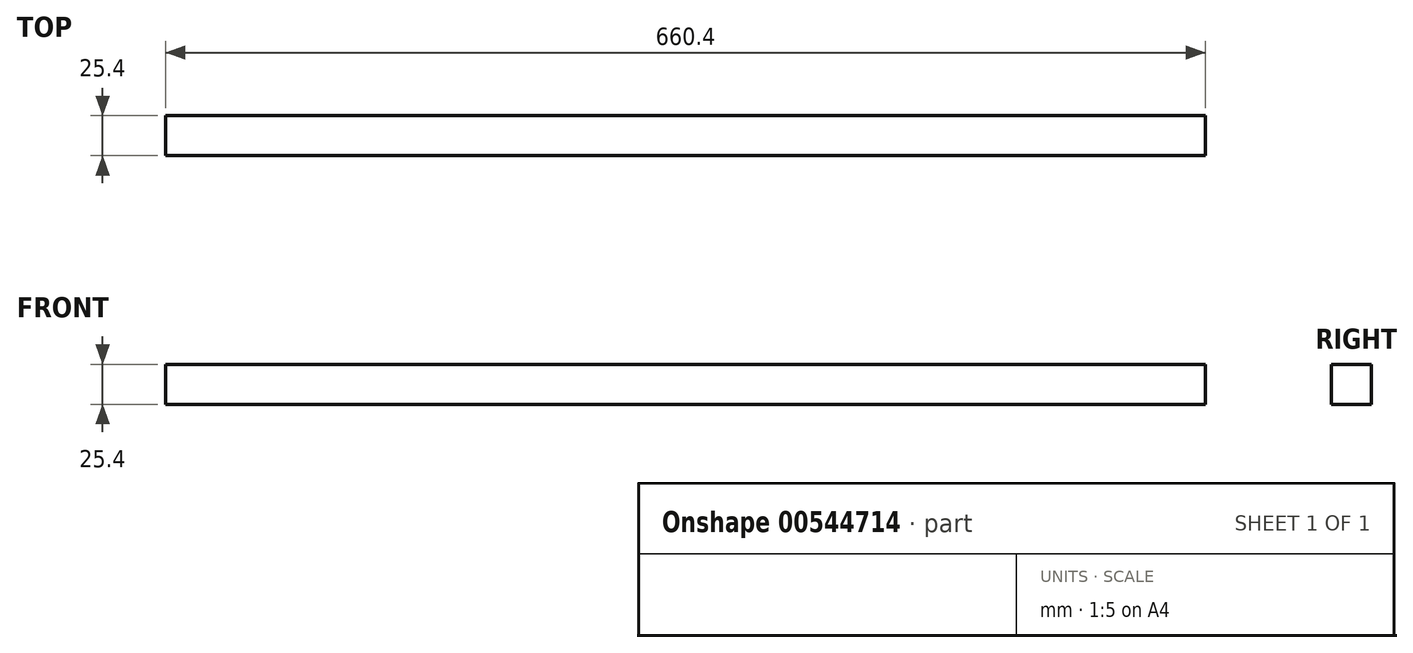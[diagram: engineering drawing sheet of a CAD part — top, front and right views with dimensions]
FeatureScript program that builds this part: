
annotation { "Feature Type Name" : "Feature", "Feature Type Description" : "" }
export const myFeature = defineFeature(function(context is Context, id is Id, definition is map)
    precondition{}
    {
        {
            var Q0;
            Q0=qCreatedBy(makeId("Top.planeOp"),FACE);
            var sketch = newSketch(context, id + "F0", { "sketchPlane" : qUnion([Q0])});
            skLineSegment(sketch, "E0.bottom", {"start": v(0, 0) * mm, "end": v(660.4, 0) * mm});
            skLineSegment(sketch, "E0.top", {"start": v(0, 25.4) * mm, "end": v(660.4, 25.4) * mm});
            skLineSegment(sketch, "E0.left", {"start": v(0, 0) * mm, "end": v(0, 25.4) * mm});
            skLineSegment(sketch, "E0.right", {"start": v(660.4, 0) * mm, "end": v(660.4, 25.4) * mm});
            skSolve(sketch);
        }
        {
            var Q0;
            Q0=makeQuery(id+"F0.imprint","IMPRINT",FACE,{"disambiguationData":[TD([[makeQuery(id+"F0.imprint","IMPRINT",EDGE,{"derivedFrom":sQuery(id+"F0.wireOp",EDGE,"E0.bottom")}),1.0]])]});
            extrude(context, id + "F1", {"entities" : qUnion([Q0]), "depth" : 25.4 * mm, "offsetDistance" : 25.4 * mm});
        }
    });
